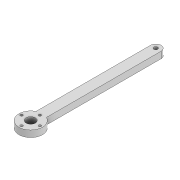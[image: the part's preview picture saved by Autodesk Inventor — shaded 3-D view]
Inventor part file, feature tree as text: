
AUTODESK INVENTOR PART (.ipt)
format: ipt  version: 2022 (Build 260153000, 153)  size: 113,664 bytes
history: native  units: mm
features: extrude x2, sketch x2, projected_geometry x1
ambient origin geometry x8: Origin, YZ Plane, XZ Plane, XY Plane, X Axis, Y Axis, Z Axis, Center Point
bodies: Solid1 (feature_tree)
feature tree (5):
  extrude  "Extrusion1"  Depth=7.1mm
  extrude  "Extrusion4"  Depth=7.0mm
  sketch  "Sketch1"  dims[d0=18.0mm d1=7.1mm]
  sketch  "Sketch4"  dims[d2=2.0mm d3=7.0mm d4=40.0mm d6=360.0deg d8=5.0mm d9=0.0mm d19=95.811mm d20=8.0mm d21=3.0mm d22=5.0mm d23=0.0mm]
  projected_geometry  "Projected Loop3"
